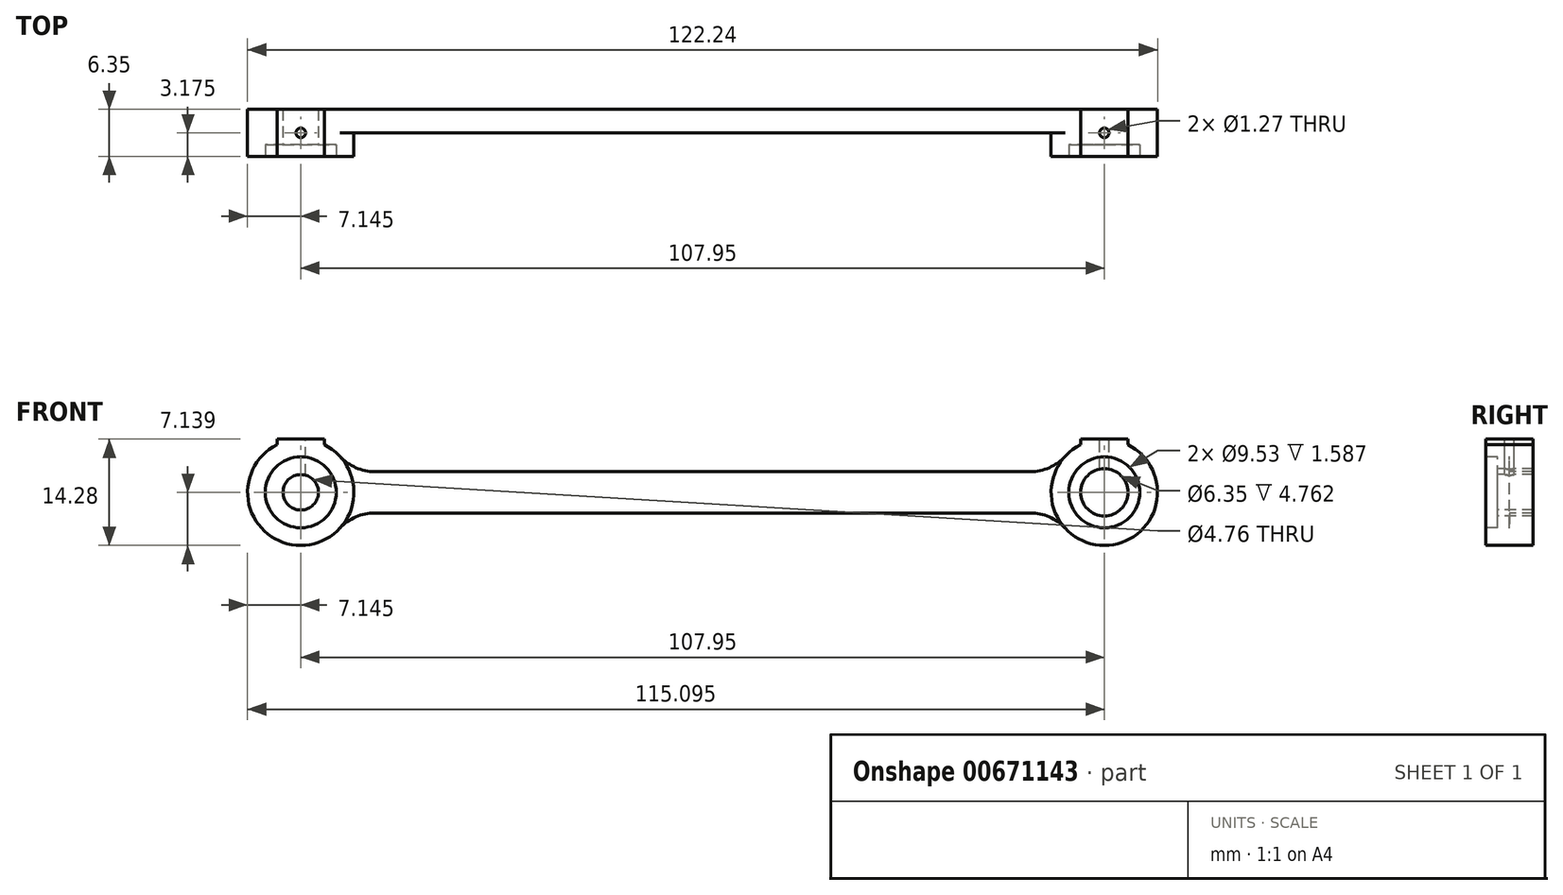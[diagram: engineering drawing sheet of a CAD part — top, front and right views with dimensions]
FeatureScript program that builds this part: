
annotation { "Feature Type Name" : "Feature", "Feature Type Description" : "" }
export const myFeature = defineFeature(function(context is Context, id is Id, definition is map)
    precondition{}
    {
        {
            var Q0;
            Q0=qCreatedBy(makeId("Front.planeOp"),FACE);
            var sketch = newSketch(context, id + "F0", { "sketchPlane" : qUnion([Q0])});
            skLineSegment(sketch, "E0", {"start": v(3.78, 14.91) * mm, "end": v(111.73, 14.91) * mm});
            skLineSegment(sketch, "E1", {"start": v(111.73, 14.91) * mm, "end": v(111.73, 20.47) * mm});
            skLineSegment(sketch, "E2", {"start": v(111.73, 20.47) * mm, "end": v(3.78, 20.47) * mm});
            skLineSegment(sketch, "E3", {"start": v(3.78, 20.47) * mm, "end": v(3.78, 14.91) * mm});
            skSolve(sketch);
        }
        {
            var Q0;
            Q0=qSketchRegion(id+"F0",true);
            extrude(context, id + "F1", {"entities" : qUnion([Q0]), "depth" : 3.17 * mm});
        }
        {
            var Q0;
            Q0=makeQuery(id+"F1.opExtrude","CAP_FACE",FACE,{"disambiguationData":[OSD([sQuery(id+"F0.wireOp",EDGE,"E0"),sQuery(id+"F0.wireOp",EDGE,"E1"),sQuery(id+"F0.wireOp",EDGE,"E2"),sQuery(id+"F0.wireOp",EDGE,"E3")])],"isStart":false});
            var sketch = newSketch(context, id + "F2", { "sketchPlane" : qUnion([Q0])});
            skCircle(sketch, "E4", {"center": v(3.78, 17.69) * mm, "radius": 7.14 * mm});
            skSolve(sketch);
        }
        {
            var Q0;
            Q0=qSketchRegion(id+"F2",true);
            extrude(context, id + "F3", {"entities" : qUnion([Q0]), "operationType" : NewBodyOperationType.ADD, "oppositeDirection" : true, "depth" : 3.17 * mm});
        }
        {
            var Q0;
            Q0=makeQuery(id+"F3.boolean.opBoolean","MERGE",FACE,{"derivedFrom":[makeQuery(id+"F1.opExtrude","CAP_FACE",FACE,{"disambiguationData":[OSD([sQuery(id+"F0.wireOp",EDGE,"E0"),sQuery(id+"F0.wireOp",EDGE,"E1"),sQuery(id+"F0.wireOp",EDGE,"E2"),sQuery(id+"F0.wireOp",EDGE,"E3")])],"isStart":false}),makeQuery(id+"F3.opExtrude","CAP_FACE",FACE,{"disambiguationData":[OSD([sQuery(id+"F2.wireOp",EDGE,"E4")])],"isStart":true})]});
            var sketch = newSketch(context, id + "F4", { "sketchPlane" : qUnion([Q0])});
            skCircle(sketch, "E5", {"center": v(3.78, 17.69) * mm, "radius": 7.14 * mm});
            skSolve(sketch);
        }
        {
            var Q0;
            Q0=qSketchRegion(id+"F4",true);
            extrude(context, id + "F5", {"entities" : qUnion([Q0]), "operationType" : NewBodyOperationType.ADD, "depth" : 3.17 * mm});
        }
        {
            var Q0;
            Q0=makeQuery(id+"F5.opExtrude","CAP_FACE",FACE,{"disambiguationData":[OSD([sQuery(id+"F4.wireOp",EDGE,"E5")])],"isStart":false});
            var sketch = newSketch(context, id + "F6", { "sketchPlane" : qUnion([Q0])});
            skCircle(sketch, "E6", {"center": v(3.78, 17.69) * mm, "radius": 2.38 * mm});
            skSolve(sketch);
        }
        {
            var Q0;
            Q0=qSketchRegion(id+"F6",true);
            extrude(context, id + "F7", {"entities" : qUnion([Q0]), "operationType" : NewBodyOperationType.REMOVE, "oppositeDirection" : true, "depth" : 25.4 * mm});
        }
        {
            var Q0;
            Q0=makeQuery(id+"F5.opExtrude","CAP_FACE",FACE,{"disambiguationData":[OSD([sQuery(id+"F4.wireOp",EDGE,"E5")])],"isStart":false});
            var sketch = newSketch(context, id + "F8", { "sketchPlane" : qUnion([Q0])});
            skCircle(sketch, "E7", {"center": v(3.78, 17.69) * mm, "radius": 4.76 * mm});
            skSolve(sketch);
        }
        {
            var Q0;
            Q0=qSketchRegion(id+"F8",true);
            extrude(context, id + "F9", {"entities" : qUnion([Q0]), "operationType" : NewBodyOperationType.REMOVE, "oppositeDirection" : true, "depth" : 1.59 * mm});
        }
        {
            var Q0;
            Q0=makeQuery(id+"F5.opExtrude","CAP_FACE",FACE,{"disambiguationData":[OSD([sQuery(id+"F4.wireOp",EDGE,"E5")])],"isStart":false});
            var sketch = newSketch(context, id + "F10", { "sketchPlane" : qUnion([Q0])});
            skLineSegment(sketch, "E8", {"start": v(-3.24, 24.83) * mm, "end": v(11.05, 24.83) * mm});
            skLineSegment(sketch, "E9", {"start": v(0.6, 24.83) * mm, "end": v(0.6, 24.09) * mm});
            skLineSegment(sketch, "E10", {"start": v(3.78, 17.69) * mm, "end": v(3.78, 24.83) * mm});
            skLineSegment(sketch, "E11", {"start": v(6.96, 24.83) * mm, "end": v(6.96, 24.09) * mm});
            skArc(sketch, "E12", {"start": v(0.6, 24.09) * mm, "mid": v(3.78, 24.83) * mm, "end": v(6.96, 24.09) * mm});
            skSolve(sketch);
        }
        {
            var Q0;
            Q0=qSketchRegion(id+"F10",true);
            extrude(context, id + "F11", {"entities" : qUnion([Q0]), "oppositeDirection" : true, "depth" : 6.35 * mm});
        }
        {
            var Q0;
            {var subQ0=sQuery(id+"F10.wireOp",EDGE,"E8");Q0=makeQuery(id+"F11.opExtrude","SWEPT_FACE",FACE,{"disambiguationData":[OSD([subQ0]),TDD([makeQuery(id+"F10.imprint","IMPRINT",EDGE,{"disambiguationData":[TD([[makeQuery(id+"F10.imprint","INTERSECT",VERTEX,{"derivedFrom":[subQ0,sQuery(id+"F10.wireOp",EDGE,"E9")]}),-1.0]])],"derivedFrom":subQ0})])]});}
            var sketch = newSketch(context, id + "F12", { "sketchPlane" : qUnion([Q0])});
            skCircle(sketch, "E13", {"center": v(3.78, -3.17) * mm, "radius": 0.64 * mm});
            skSolve(sketch);
        }
        {
            var Q0;
            Q0=makeQuery(id+"F1.opExtrude","SWEPT_BODY",BODY,{"disambiguationData":[OSD([sQuery(id+"F0.wireOp",EDGE,"E0"),sQuery(id+"F0.wireOp",EDGE,"E1"),sQuery(id+"F0.wireOp",EDGE,"E2"),sQuery(id+"F0.wireOp",EDGE,"E3")])]});
            var Q1;
            Q1=makeQuery(id+"F11.opExtrude","SWEPT_BODY",BODY,{"disambiguationData":[OSD([sQuery(id+"F10.wireOp",EDGE,"E8"),sQuery(id+"F10.wireOp",EDGE,"E9"),sQuery(id+"F10.wireOp",EDGE,"E12")])]});
            var Q2;
            Q2=makeQuery(id+"F11.opExtrude","SWEPT_BODY",BODY,{"disambiguationData":[OSD([sQuery(id+"F10.wireOp",EDGE,"E8"),sQuery(id+"F10.wireOp",EDGE,"E11"),sQuery(id+"F10.wireOp",EDGE,"E12")])]});
            booleanBodies(context, id + "F13", {"operationType" : BooleanOperationType.UNION, "tools" : qUnion([Q0, Q1, Q2])});
        }
        {
            var Q0;
            {var subQ0=sQuery(id+"F12.wireOp",EDGE,"E13");var subQ1=sQuery(id+"F10.wireOp",EDGE,"E12");var subQ2=sQuery(id+"F10.wireOp",EDGE,"E8");var subQ3=makeQuery(id+"F11.opExtrude","SWEPT_EDGE",EDGE,{"disambiguationData":[OSD([subQ2,subQ1]),ownerDisambiguation([makeQuery(id+"F11.opExtrude","SWEPT_BODY",BODY,{"disambiguationData":[OSD([subQ2,sQuery(id+"F10.wireOp",EDGE,"E9"),subQ1])]})])]});var subQ4=makeQuery(id+"F12.imprint","INTERSECT",VERTEX,{"disambiguationData":[OD(0.0)],"derivedFrom":[subQ3,subQ0]});Q0=makeQuery(id+"F12.imprint","IMPRINT",FACE,{"disambiguationData":[TD([[makeQuery(id+"F12.imprint","IMPRINT",EDGE,{"disambiguationData":[TD([[subQ4,1.0]])],"derivedFrom":subQ0}),1.0]])]});}
            var Q1;
            {var subQ0=sQuery(id+"F12.wireOp",EDGE,"E13");var subQ1=sQuery(id+"F10.wireOp",EDGE,"E12");var subQ2=sQuery(id+"F10.wireOp",EDGE,"E8");var subQ3=makeQuery(id+"F11.opExtrude","SWEPT_EDGE",EDGE,{"disambiguationData":[OSD([subQ2,subQ1]),ownerDisambiguation([makeQuery(id+"F11.opExtrude","SWEPT_BODY",BODY,{"disambiguationData":[OSD([subQ2,sQuery(id+"F10.wireOp",EDGE,"E9"),subQ1])]})])]});var subQ4=makeQuery(id+"F12.imprint","INTERSECT",VERTEX,{"disambiguationData":[OD(0.0)],"derivedFrom":[subQ3,subQ0]});Q1=makeQuery(id+"F12.imprint","IMPRINT",FACE,{"disambiguationData":[TD([[makeQuery(id+"F12.imprint","IMPRINT",EDGE,{"disambiguationData":[TD([[subQ4,-1.0]])],"derivedFrom":subQ0}),1.0]])]});}
            extrude(context, id + "F14", {"entities" : qUnion([Q0, Q1]), "operationType" : NewBodyOperationType.REMOVE, "oppositeDirection" : true, "depth" : 6.35 * mm});
        }
        {
            var Q0;
            Q0=makeQuery(id+"F3.boolean.opBoolean","MERGE",FACE,{"derivedFrom":[makeQuery(id+"F1.opExtrude","CAP_FACE",FACE,{"disambiguationData":[OSD([sQuery(id+"F0.wireOp",EDGE,"E0"),sQuery(id+"F0.wireOp",EDGE,"E1"),sQuery(id+"F0.wireOp",EDGE,"E2"),sQuery(id+"F0.wireOp",EDGE,"E3")])],"isStart":false}),makeQuery(id+"F3.opExtrude","CAP_FACE",FACE,{"disambiguationData":[OSD([sQuery(id+"F2.wireOp",EDGE,"E4")])],"isStart":true})]});
            var sketch = newSketch(context, id + "F15", { "sketchPlane" : qUnion([Q0])});
            skCircle(sketch, "E14", {"center": v(111.73, 17.69) * mm, "radius": 7.14 * mm});
            skSolve(sketch);
        }
        {
            var Q0;
            Q0=qSketchRegion(id+"F15",true);
            extrude(context, id + "F16", {"entities" : qUnion([Q0]), "operationType" : NewBodyOperationType.ADD, "oppositeDirection" : true, "depth" : 3.17 * mm});
        }
        {
            var Q0;
            Q0=makeQuery(id+"F16.boolean.opBoolean","MERGE",FACE,{"derivedFrom":[makeQuery(id+"F3.boolean.opBoolean","MERGE",FACE,{"derivedFrom":[makeQuery(id+"F1.opExtrude","CAP_FACE",FACE,{"disambiguationData":[OSD([sQuery(id+"F0.wireOp",EDGE,"E0"),sQuery(id+"F0.wireOp",EDGE,"E1"),sQuery(id+"F0.wireOp",EDGE,"E2"),sQuery(id+"F0.wireOp",EDGE,"E3")])],"isStart":false}),makeQuery(id+"F3.opExtrude","CAP_FACE",FACE,{"disambiguationData":[OSD([sQuery(id+"F2.wireOp",EDGE,"E4")])],"isStart":true})]}),makeQuery(id+"F16.opExtrude","CAP_FACE",FACE,{"disambiguationData":[OSD([sQuery(id+"F15.wireOp",EDGE,"E14")])],"isStart":true})]});
            var sketch = newSketch(context, id + "F17", { "sketchPlane" : qUnion([Q0])});
            skCircle(sketch, "E15", {"center": v(111.73, 17.69) * mm, "radius": 7.14 * mm});
            skSolve(sketch);
        }
        {
            var Q0;
            Q0=qSketchRegion(id+"F17",true);
            extrude(context, id + "F18", {"entities" : qUnion([Q0]), "operationType" : NewBodyOperationType.ADD, "depth" : 3.17 * mm});
        }
        {
            var Q0;
            Q0=makeQuery(id+"F18.opExtrude","CAP_FACE",FACE,{"disambiguationData":[OSD([sQuery(id+"F17.wireOp",EDGE,"E15")])],"isStart":false});
            var sketch = newSketch(context, id + "F19", { "sketchPlane" : qUnion([Q0])});
            skCircle(sketch, "E16", {"center": v(111.73, 17.69) * mm, "radius": 3.18 * mm});
            skSolve(sketch);
        }
        {
            var Q0;
            Q0=qSketchRegion(id+"F19",true);
            extrude(context, id + "F20", {"entities" : qUnion([Q0]), "operationType" : NewBodyOperationType.REMOVE, "oppositeDirection" : true, "depth" : 25.4 * mm});
        }
        {
            var Q0;
            Q0=makeQuery(id+"F18.opExtrude","CAP_FACE",FACE,{"disambiguationData":[OSD([sQuery(id+"F17.wireOp",EDGE,"E15")])],"isStart":false});
            var sketch = newSketch(context, id + "F21", { "sketchPlane" : qUnion([Q0])});
            skCircle(sketch, "E17", {"center": v(111.73, 17.69) * mm, "radius": 4.76 * mm});
            skSolve(sketch);
        }
        {
            var Q0;
            Q0=qSketchRegion(id+"F21",true);
            extrude(context, id + "F22", {"entities" : qUnion([Q0]), "operationType" : NewBodyOperationType.REMOVE, "oppositeDirection" : true, "depth" : 1.59 * mm});
        }
        {
            var Q0;
            Q0=makeQuery(id+"F18.opExtrude","CAP_FACE",FACE,{"disambiguationData":[OSD([sQuery(id+"F17.wireOp",EDGE,"E15")])],"isStart":false});
            var sketch = newSketch(context, id + "F23", { "sketchPlane" : qUnion([Q0])});
            skLineSegment(sketch, "E18", {"start": v(103.62, 24.83) * mm, "end": v(118.22, 24.83) * mm});
            skLineSegment(sketch, "E19", {"start": v(108.56, 24.83) * mm, "end": v(108.56, 24.09) * mm});
            skLineSegment(sketch, "E20", {"start": v(114.9, 24.83) * mm, "end": v(114.9, 24.09) * mm});
            skLineSegment(sketch, "E21", {"start": v(111.73, 17.69) * mm, "end": v(111.73, 24.83) * mm});
            skArc(sketch, "E22", {"start": v(108.56, 24.09) * mm, "mid": v(111.73, 24.83) * mm, "end": v(114.9, 24.09) * mm});
            skSolve(sketch);
        }
        {
            var Q0;
            Q0=qSketchRegion(id+"F23",true);
            extrude(context, id + "F24", {"entities" : qUnion([Q0]), "operationType" : NewBodyOperationType.ADD, "oppositeDirection" : true, "depth" : 6.35 * mm});
        }
        {
            var Q0;
            {var subQ0=sQuery(id+"F23.wireOp",EDGE,"E18");Q0=makeQuery(id+"F24.boolean.opBoolean","MERGE",FACE,{"derivedFrom":[makeQuery(id+"F24.opExtrude","SWEPT_FACE",FACE,{"disambiguationData":[OSD([subQ0]),TDD([makeQuery(id+"F23.imprint","IMPRINT",EDGE,{"disambiguationData":[TD([[makeQuery(id+"F23.imprint","INTERSECT",VERTEX,{"derivedFrom":[subQ0,sQuery(id+"F23.wireOp",EDGE,"E19")]}),-1.0]])],"derivedFrom":subQ0})])]}),makeQuery(id+"F24.opExtrude","SWEPT_FACE",FACE,{"disambiguationData":[OSD([subQ0]),TDD([makeQuery(id+"F23.imprint","IMPRINT",EDGE,{"disambiguationData":[TD([[makeQuery(id+"F23.imprint","INTERSECT",VERTEX,{"derivedFrom":[subQ0,sQuery(id+"F23.wireOp",EDGE,"E20")]}),1.0]])],"derivedFrom":subQ0})])]})]});}
            var sketch = newSketch(context, id + "F25", { "sketchPlane" : qUnion([Q0])});
            skCircle(sketch, "E23", {"center": v(111.73, -3.18) * mm, "radius": 0.64 * mm});
            skSolve(sketch);
        }
        {
            var Q0;
            Q0=qSketchRegion(id+"F25",true);
            extrude(context, id + "F26", {"entities" : qUnion([Q0]), "operationType" : NewBodyOperationType.REMOVE, "oppositeDirection" : true, "depth" : 6.35 * mm});
        }
        {
            var Q0;
            Q0=makeQuery(id+"F3.boolean.opBoolean","INTERSECT",EDGE,{"derivedFrom":[makeQuery(id+"F1.opExtrude","SWEPT_FACE",FACE,{"disambiguationData":[OSD([sQuery(id+"F0.wireOp",EDGE,"E2")])]}),makeQuery(id+"F3.opExtrude","SWEPT_FACE",FACE,{"disambiguationData":[OSD([sQuery(id+"F2.wireOp",EDGE,"E4")])]})]});
            var Q1;
            Q1=makeQuery(id+"F3.boolean.opBoolean","INTERSECT",EDGE,{"derivedFrom":[makeQuery(id+"F1.opExtrude","SWEPT_FACE",FACE,{"disambiguationData":[OSD([sQuery(id+"F0.wireOp",EDGE,"E0")])]}),makeQuery(id+"F3.opExtrude","SWEPT_FACE",FACE,{"disambiguationData":[OSD([sQuery(id+"F2.wireOp",EDGE,"E4")])]})]});
            var Q2;
            Q2=makeQuery(id+"F16.boolean.opBoolean","INTERSECT",EDGE,{"derivedFrom":[makeQuery(id+"F1.opExtrude","SWEPT_FACE",FACE,{"disambiguationData":[OSD([sQuery(id+"F0.wireOp",EDGE,"E2")])]}),makeQuery(id+"F16.opExtrude","SWEPT_FACE",FACE,{"disambiguationData":[OSD([sQuery(id+"F15.wireOp",EDGE,"E14")])]})]});
            var Q3;
            Q3=makeQuery(id+"F16.boolean.opBoolean","INTERSECT",EDGE,{"derivedFrom":[makeQuery(id+"F1.opExtrude","SWEPT_FACE",FACE,{"disambiguationData":[OSD([sQuery(id+"F0.wireOp",EDGE,"E0")])]}),makeQuery(id+"F16.opExtrude","SWEPT_FACE",FACE,{"disambiguationData":[OSD([sQuery(id+"F15.wireOp",EDGE,"E14")])]})]});
            var Q4;
            Q4=makeQuery(id+"F11.opExtrude","SWEPT_EDGE",EDGE,{"disambiguationData":[OSD([sQuery(id+"F4.wireOp",EDGE,"E5"),sQuery(id+"F10.wireOp",EDGE,"E11"),sQuery(id+"F10.wireOp",EDGE,"E12")])]});
            var Q5;
            Q5=makeQuery(id+"F11.opExtrude","SWEPT_EDGE",EDGE,{"disambiguationData":[OSD([sQuery(id+"F4.wireOp",EDGE,"E5"),sQuery(id+"F10.wireOp",EDGE,"E9"),sQuery(id+"F10.wireOp",EDGE,"E12")])]});
            var Q6;
            Q6=makeQuery(id+"F24.opExtrude","SWEPT_EDGE",EDGE,{"disambiguationData":[OSD([sQuery(id+"F17.wireOp",EDGE,"E15"),sQuery(id+"F23.wireOp",EDGE,"E19"),sQuery(id+"F23.wireOp",EDGE,"E22")])]});
            var Q7;
            Q7=makeQuery(id+"F24.opExtrude","SWEPT_EDGE",EDGE,{"disambiguationData":[OSD([sQuery(id+"F17.wireOp",EDGE,"E15"),sQuery(id+"F23.wireOp",EDGE,"E20"),sQuery(id+"F23.wireOp",EDGE,"E22")])]});
            fillet(context, id + "F27", {"entities" : qUnion([Q0, Q1, Q2, Q3, Q4, Q5, Q6, Q7]), "radius" : 6.35 * mm, "tangentPropagation" : true, "allowEdgeOverflow" : false});
        }
    });
